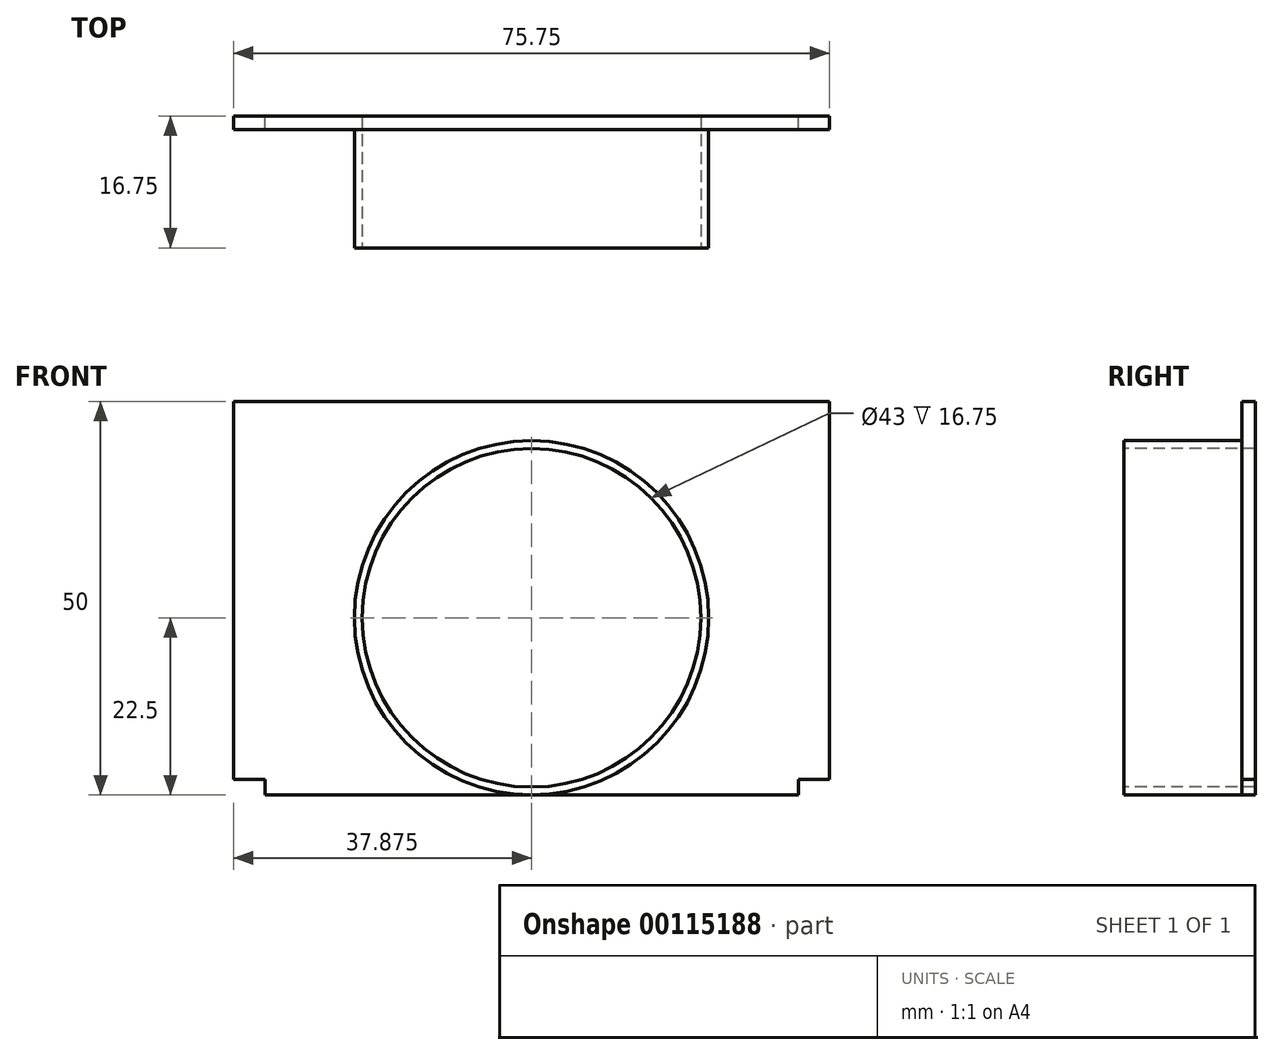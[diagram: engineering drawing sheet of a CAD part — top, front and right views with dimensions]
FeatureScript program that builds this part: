
annotation { "Feature Type Name" : "Feature", "Feature Type Description" : "" }
export const myFeature = defineFeature(function(context is Context, id is Id, definition is map)
    precondition{}
    {
        {
            var Q0;
            Q0=qCreatedBy(makeId("Front.planeOp"),FACE);
            var sketch = newSketch(context, id + "F0", { "sketchPlane" : qUnion([Q0])});
            skLineSegment(sketch, "E0", {"start": v(0, 0) * mm, "end": v(75.75, 0) * mm});
            skLineSegment(sketch, "E1", {"start": v(75.75, 0) * mm, "end": v(75.75, -48) * mm});
            skLineSegment(sketch, "E2", {"start": v(75.75, -48) * mm, "end": v(71.75, -48) * mm});
            skLineSegment(sketch, "E3", {"start": v(71.75, -48) * mm, "end": v(71.75, -50) * mm});
            skLineSegment(sketch, "E4", {"start": v(71.75, -50) * mm, "end": v(4, -50) * mm});
            skLineSegment(sketch, "E5", {"start": v(4, -50) * mm, "end": v(4, -48) * mm});
            skLineSegment(sketch, "E6", {"start": v(4, -48) * mm, "end": v(0, -48) * mm});
            skLineSegment(sketch, "E7", {"start": v(0, -48) * mm, "end": v(0, 0) * mm});
            skSolve(sketch);
        }
        {
            var Q0;
            Q0=makeQuery(id+"F0.imprint","IMPRINT",FACE,{"disambiguationData":[TD([[makeQuery(id+"F0.imprint","IMPRINT",EDGE,{"derivedFrom":sQuery(id+"F0.wireOp",EDGE,"E0")}),-1.0]])]});
            extrude(context, id + "F1", {"entities" : qUnion([Q0]), "depth" : 1.75 * mm});
        }
        {
            var Q0;
            Q0=makeQuery(id+"F1.opExtrude","CAP_FACE",FACE,{"disambiguationData":[OSD([sQuery(id+"F0.wireOp",EDGE,"E0"),sQuery(id+"F0.wireOp",EDGE,"E1"),sQuery(id+"F0.wireOp",EDGE,"E2"),sQuery(id+"F0.wireOp",EDGE,"E3"),sQuery(id+"F0.wireOp",EDGE,"E4"),sQuery(id+"F0.wireOp",EDGE,"E5"),sQuery(id+"F0.wireOp",EDGE,"E6"),sQuery(id+"F0.wireOp",EDGE,"E7")])],"isStart":false});
            var sketch = newSketch(context, id + "F2", { "sketchPlane" : qUnion([Q0])});
            skCircle(sketch, "E8", {"center": v(37.87, -27.5) * mm, "radius": 21.5 * mm});
            skSolve(sketch);
        }
        {
            var Q0;
            Q0=makeQuery(id+"F2.imprint","IMPRINT",FACE,{"disambiguationData":[TD([[makeQuery(id+"F2.imprint","IMPRINT",EDGE,{"derivedFrom":sQuery(id+"F2.wireOp",EDGE,"E8")}),1.0]])]});
            extrude(context, id + "F3", {"entities" : qUnion([Q0]), "operationType" : NewBodyOperationType.REMOVE, "oppositeDirection" : true, "depth" : 25 * mm});
        }
        {
            var Q0;
            Q0=makeQuery(id+"F1.opExtrude","CAP_FACE",FACE,{"disambiguationData":[OSD([sQuery(id+"F0.wireOp",EDGE,"E0"),sQuery(id+"F0.wireOp",EDGE,"E1"),sQuery(id+"F0.wireOp",EDGE,"E2"),sQuery(id+"F0.wireOp",EDGE,"E3"),sQuery(id+"F0.wireOp",EDGE,"E4"),sQuery(id+"F0.wireOp",EDGE,"E5"),sQuery(id+"F0.wireOp",EDGE,"E6"),sQuery(id+"F0.wireOp",EDGE,"E7")])],"isStart":false});
            var sketch = newSketch(context, id + "F4", { "sketchPlane" : qUnion([Q0])});
            skCircle(sketch, "E9", {"center": v(37.87, -27.5) * mm, "radius": 22.5 * mm});
            skSolve(sketch);
        }
        {
            var Q0;
            Q0=makeQuery(id+"F4.imprint","IMPRINT",FACE,{"disambiguationData":[TD([[makeQuery(id+"F4.imprint","IMPRINT",EDGE,{"derivedFrom":sQuery(id+"F4.wireOp",EDGE,"E9")}),1.0]])]});
            extrude(context, id + "F5", {"entities" : qUnion([Q0]), "operationType" : NewBodyOperationType.ADD, "depth" : 15 * mm});
        }
    });
